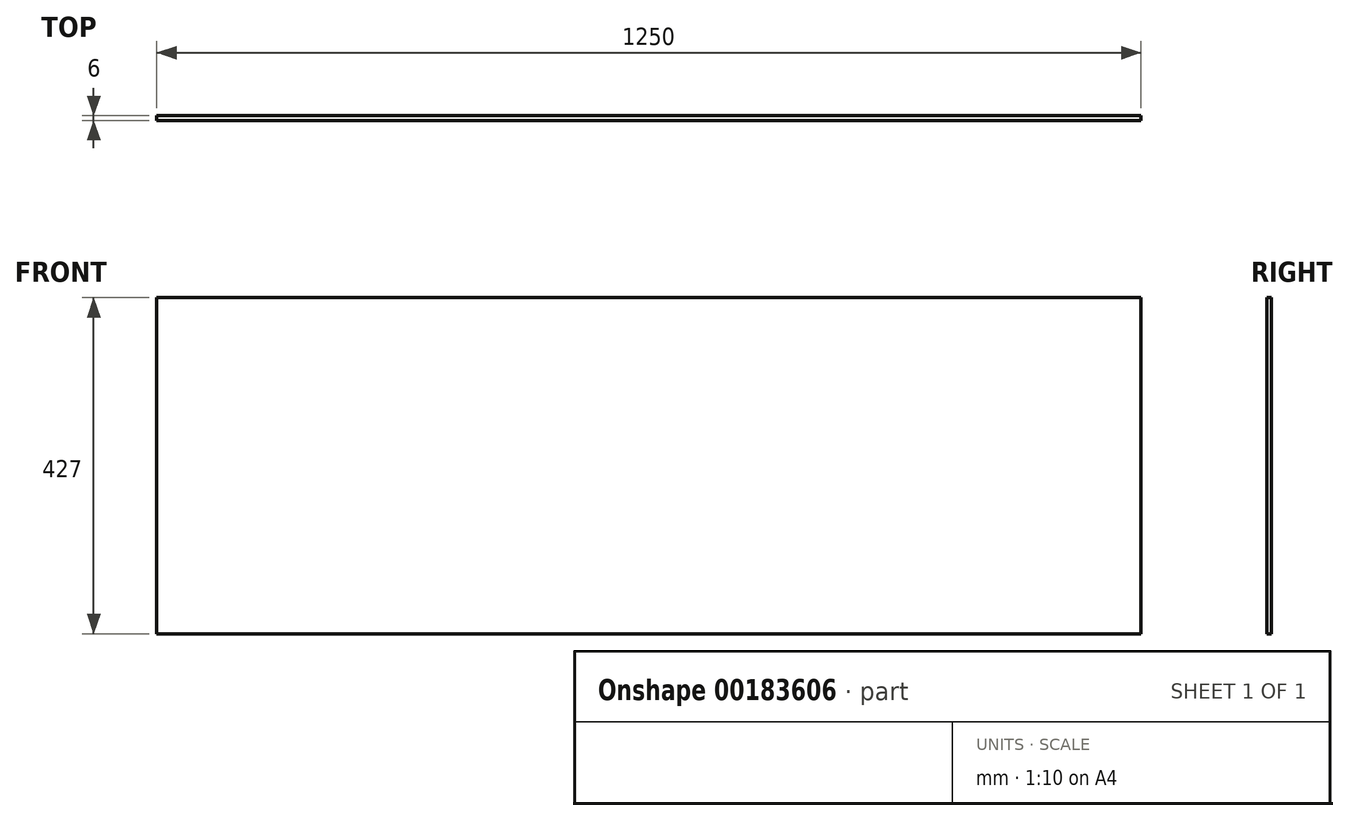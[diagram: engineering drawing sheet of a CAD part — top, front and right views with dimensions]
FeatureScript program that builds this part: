
annotation { "Feature Type Name" : "Feature", "Feature Type Description" : "" }
export const myFeature = defineFeature(function(context is Context, id is Id, definition is map)
    precondition{}
    {
        {
            var Q0;
            Q0=qCreatedBy(makeId("Front.planeOp"),FACE);
            var sketch = newSketch(context, id + "F0", { "sketchPlane" : qUnion([Q0])});
            skLineSegment(sketch, "E0.bottom", {"start": v(625, 213.5) * mm, "end": v(-625, 213.5) * mm});
            skLineSegment(sketch, "E0.top", {"start": v(625, -213.5) * mm, "end": v(-625, -213.5) * mm});
            skLineSegment(sketch, "E0.left", {"start": v(625, 213.5) * mm, "end": v(625, -213.5) * mm});
            skLineSegment(sketch, "E0.right", {"start": v(-625, 213.5) * mm, "end": v(-625, -213.5) * mm});
            skPoint(sketch, "E0.middle", {"position": v(0, 0) * mm});
            skSolve(sketch);
        }
        {
            var Q0;
            Q0 = qSketchRegion(id + "F0", true);
            extrude(context, id + "F1", {"entities" : qUnion([Q0]), "depth" : 6 * mm});
        }
    });
